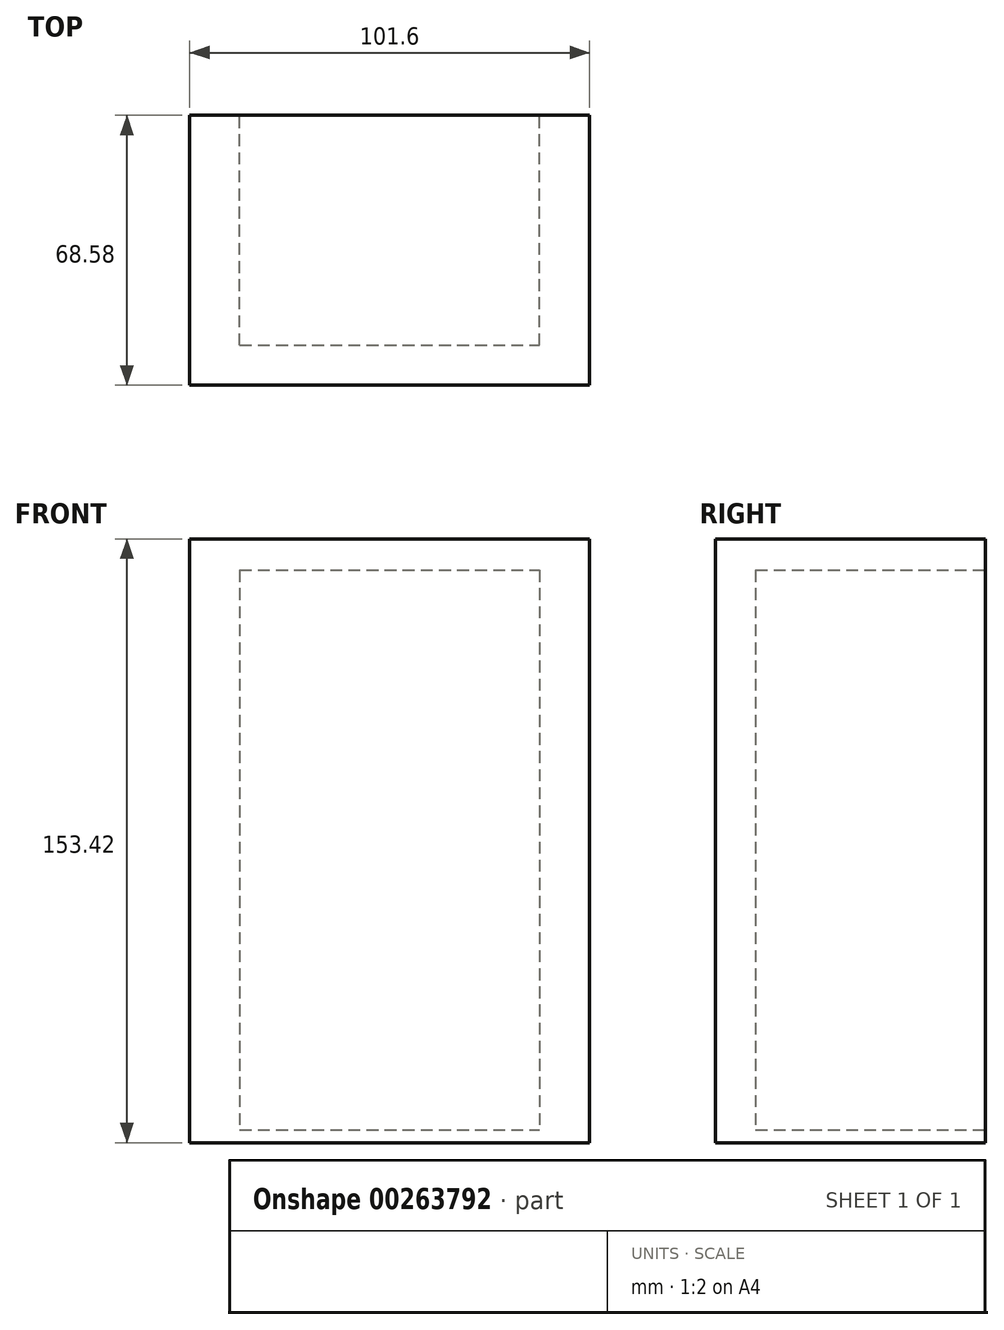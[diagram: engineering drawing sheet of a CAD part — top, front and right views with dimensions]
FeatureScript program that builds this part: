
annotation { "Feature Type Name" : "Feature", "Feature Type Description" : "" }
export const myFeature = defineFeature(function(context is Context, id is Id, definition is map)
    precondition{}
    {
        {
            var Q0;
            Q0=qCreatedBy(makeId("Top.planeOp"),FACE);
            var sketch = newSketch(context, id + "F0", { "sketchPlane" : qUnion([Q0])});
            skLineSegment(sketch, "E0.bottom", {"start": v(50.8, 34.3) * mm, "end": v(-50.8, 34.3) * mm});
            skLineSegment(sketch, "E0.top", {"start": v(50.8, -34.3) * mm, "end": v(-50.8, -34.3) * mm});
            skLineSegment(sketch, "E0.left", {"start": v(50.8, 34.3) * mm, "end": v(50.8, -34.3) * mm});
            skLineSegment(sketch, "E0.right", {"start": v(-50.8, 34.3) * mm, "end": v(-50.8, -34.3) * mm});
            skPoint(sketch, "E0.middle", {"position": v(0, 0) * mm});
            skSolve(sketch);
        }
        {
            var Q0;
            Q0 = qSketchRegion(id + "F0", true);
            extrude(context, id + "F1", {"entities" : qUnion([Q0]), "depth" : 153.42 * mm});
        }
        {
            var Q0;
            Q0=makeQuery(id+"F1.opExtrude","SWEPT_FACE",FACE,{"disambiguationData":[OSD([sQuery(id+"F0.wireOp",EDGE,"E0.bottom")])]});
            var sketch = newSketch(context, id + "F2", { "sketchPlane" : qUnion([Q0])});
            skLineSegment(sketch, "E1.bottom", {"start": v(38.1, 145.47) * mm, "end": v(-38.1, 145.47) * mm});
            skLineSegment(sketch, "E1.top", {"start": v(38.1, 3.23) * mm, "end": v(-38.1, 3.23) * mm});
            skLineSegment(sketch, "E1.left", {"start": v(38.1, 145.47) * mm, "end": v(38.1, 3.23) * mm});
            skLineSegment(sketch, "E1.right", {"start": v(-38.1, 145.47) * mm, "end": v(-38.1, 3.23) * mm});
            skPoint(sketch, "E1.middle", {"position": v(0, 74.35) * mm});
            skSolve(sketch);
        }
        {
            var Q0;
            Q0 = qSketchRegion(id + "F2", true);
            extrude(context, id + "F3", {"entities" : qUnion([Q0]), "operationType" : NewBodyOperationType.REMOVE, "oppositeDirection" : true, "depth" : 58.42 * mm});
        }
    });
